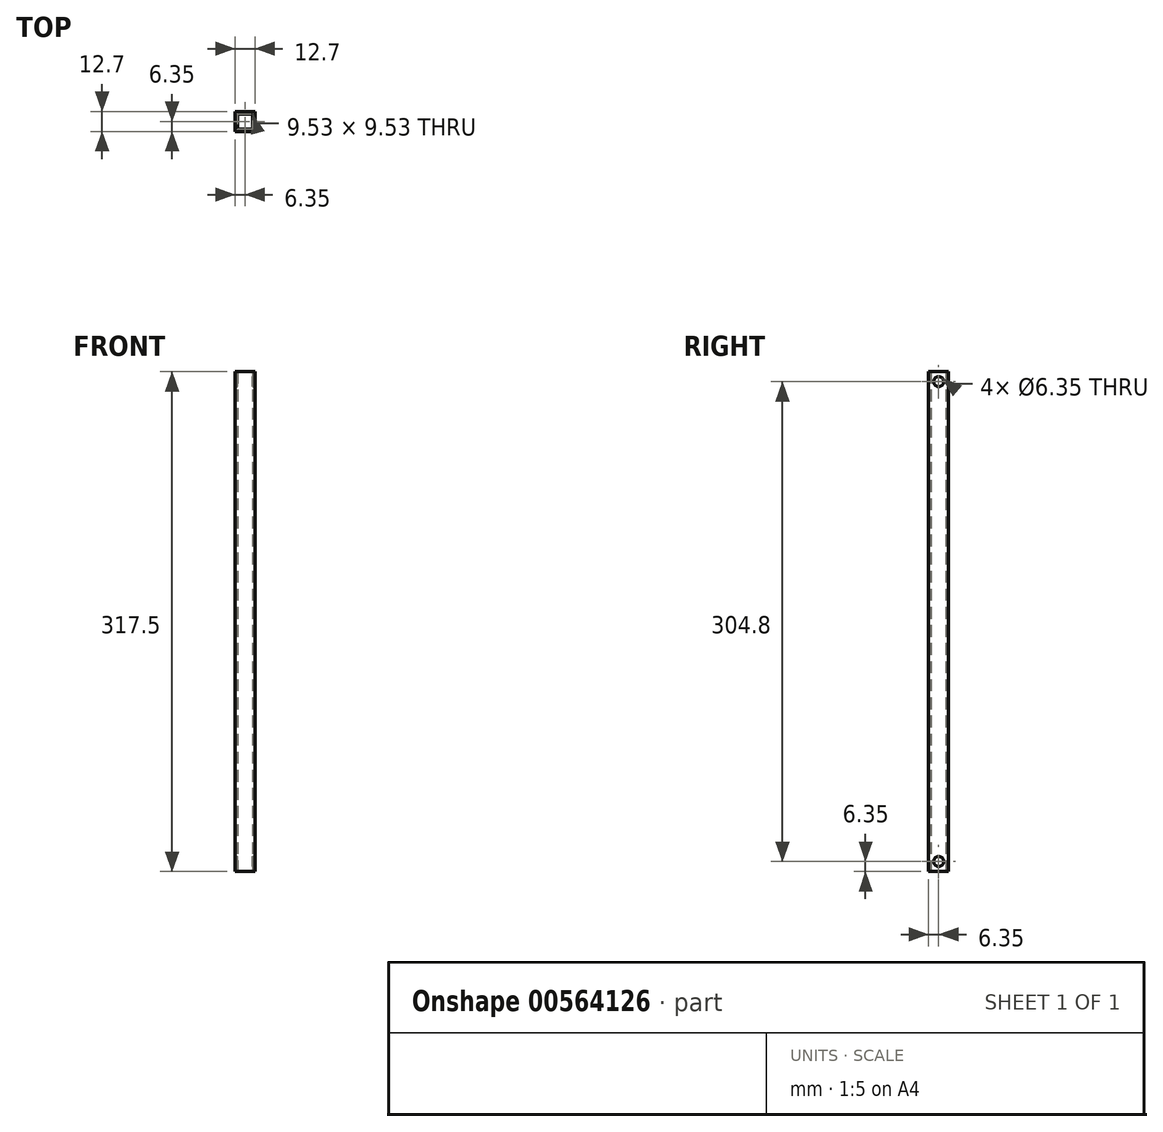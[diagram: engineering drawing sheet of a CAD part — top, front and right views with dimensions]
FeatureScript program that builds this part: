
annotation { "Feature Type Name" : "Feature", "Feature Type Description" : "" }
export const myFeature = defineFeature(function(context is Context, id is Id, definition is map)
    precondition{}
    {
        {
            var Q0;
            Q0=qCreatedBy(makeId("Top.planeOp"),FACE);
            var sketch = newSketch(context, id + "F0", { "sketchPlane" : qUnion([Q0])});
            skLineSegment(sketch, "E0.bottom", {"start": v(4.76, 4.76) * mm, "end": v(-4.76, 4.76) * mm});
            skLineSegment(sketch, "E0.top", {"start": v(4.76, -4.76) * mm, "end": v(-4.76, -4.76) * mm});
            skLineSegment(sketch, "E0.left", {"start": v(4.76, 4.76) * mm, "end": v(4.76, -4.76) * mm});
            skLineSegment(sketch, "E0.right", {"start": v(-4.76, 4.76) * mm, "end": v(-4.76, -4.76) * mm});
            skPoint(sketch, "E0.middle", {"position": v(0, 0) * mm});
            skLineSegment(sketch, "E1.bottom", {"start": v(6.35, 6.35) * mm, "end": v(-6.35, 6.35) * mm});
            skLineSegment(sketch, "E1.top", {"start": v(6.35, -6.35) * mm, "end": v(-6.35, -6.35) * mm});
            skLineSegment(sketch, "E1.left", {"start": v(6.35, 6.35) * mm, "end": v(6.35, -6.35) * mm});
            skLineSegment(sketch, "E1.right", {"start": v(-6.35, 6.35) * mm, "end": v(-6.35, -6.35) * mm});
            skLineSegment(sketch, "E2", {"start": v(0, 4.76) * mm, "end": v(0, 6.35) * mm});
            skLineSegment(sketch, "E3", {"start": v(4.76, 0) * mm, "end": v(6.35, 0) * mm});
            skSolve(sketch);
        }
        {
            var Q0;
            Q0 = qSketchRegion(id + "F0", true);
            extrude(context, id + "F1", {"entities" : qUnion([Q0]), "depth" : 317.5 * mm, "offsetDistance" : 25.4 * mm});
        }
        {
            var Q0;
            Q0=makeQuery(id+"F1.opExtrude","SWEPT_FACE",FACE,{"disambiguationData":[OSD([sQuery(id+"F0.wireOp",EDGE,"E1.left")])]});
            var sketch = newSketch(context, id + "F2", { "sketchPlane" : qUnion([Q0])});
            skCircle(sketch, "E4", {"center": v(0, 6.35) * mm, "radius": 3.18 * mm});
            skCircle(sketch, "E5", {"center": v(0, 311.15) * mm, "radius": 3.18 * mm});
            skSolve(sketch);
        }
        {
            var Q0;
            Q0 = qSketchRegion(id + "F2", true);
            extrude(context, id + "F3", {"entities" : qUnion([Q0]), "operationType" : NewBodyOperationType.REMOVE, "endBound" : BoundingType.THROUGH_ALL, "oppositeDirection" : true, "depth" : 25.4 * mm, "offsetDistance" : 25.4 * mm});
        }
    });
